# Revit family: g-2017_Fontaneria_FV-SA_Arizona-0181-B1_Monomando-Lavatorio
name_source: partatom
category: Plumbing Fixtures
revit_build: Autodesk Revit 2017 (Build: 20171027_0315(x64)
units: mm (PartAtom-declared; Revit-internal decimal feet)

## family parameters
Always vertical = Yes
Cut with Voids When Loaded = No
OmniClass Number = 23.45.55.17
OmniClass Title = Mixing Faucets
Part Type = Normal
Room Calculation Point = No
Round Connector Dimension = Use Diameter
Shared = No
Work Plane-Based = No

## types (1)
- g-2017_Fontaneria_FV-SA_Arizona-0181-B1_Monomando-Lavatorio
    AcidificacionAtmosferica = 0
    AcidificacionAtmosfericaPorUnidad = 0
    AguaConsumida = 0
    AguaConsumidaPorUnidad = 0
    Altura = 81 mm  [stored 0.265748 ft]
    Autor = Bimetica Parametric Design Services S.L.
    Bimetica = http://www.bimetica.com
    CambioClimatico = 0
    CambioClimaticoPorUnidad = 0
    ContenidoGarantia = 5 años
    CosteEnergeticoKwh = 0
    CosteEnergeticoMj = 0 J
    CosteMantenimiento = 0
    Description = Juego monocomando para lavatorio
    DestruccionCapaOzonoEstratosferica = 0
    DestruccionCapaOzonoEstratosfericaPorUnidad = 0
    Distancia Grifo de llaves = 100 mm  [stored 0.328084 ft]
    EmisionCO2 = 0
    EnergiaNoRenovableConsumida = 0
    EnergiaNoRenovableConsumidaPorUnidad = 0
    EnergiaPrimariaTotalConsumidaPorUnidad = 0
    EnergiaRenovableConsumida = 0
    EnergiaRenovableConsumidaPorUnidad = 0
    Eutrofizacion = 0
    EutrofizacionPorUnidad = 0
    FaltaDeRecursos = 0
    FaltaDeRecursosPorUnidad = 0
    FechaEmisionElementoBIM = 30/08/2018
    FechaVencimientoElementoBIM = 30/08/2019
    Flujo Agua Caliente = 0.0 L/s
    Flujo Agua Fria = 0.0 L/s
    Flujo Desagüe = 0.0 L/s
    FormacionFotoquimicaOzono = 0
    FormacionFotoquimicaOzonoPorUnidad = 0
    GarantiaExtendida = No
    IFCClasificacion = IfcValve
    InformacionTecnica = http://www.fvsa.com
    Manufacturer = FV S.A.
    MasaSuperficialKgm2 = 0
    MasterformatCodigo = 22 41 39
    MasterformatTitulo = Residential Faucets, Supplies, and Trim
    MateriaPrima = 0.00%
    Material = Acero, Cromado
    Model = B1 Arizona
    NumeroSerie = 0181/L2
    OmniclassCodigo = 23-31 11 19
    OmniclassTitulo = Faucet Mixing Valves
    Referencia = 0181/B1
    ResiduoInerte = 0
    ResiduoInertePorUnidad = 0
    ResiduoRadioactivo = 0
    ResiduoRadioactivoPorUnidad = 0
    ResiduosNoPeligrosos  = 0
    ResiduosNoPeligrososPorUnidad = 0
    ResiduosPeligrosos  = 0
    ResiduosPeligrososPorUnidad = 0
    TelefonoContacto = 0810-555-5300
    Type Comments = Apto para calefón y/o termotanque.
    UNSPSCCodigo = 30181700
    UNSPSCTitulo = Faucets or taps
    URL = http://www.fvsa.com
    URLProducto = http://www.fvsa.com
    Uniclass2.0Codigo = 40-30-96-06
    Uniclass2.0Titulo = Bath manual valves
    VersionElementoBIM = V01

note: [stored X ft] marks values corroborated as IEEE doubles in the binary element streams (Revit-internal decimal feet)
